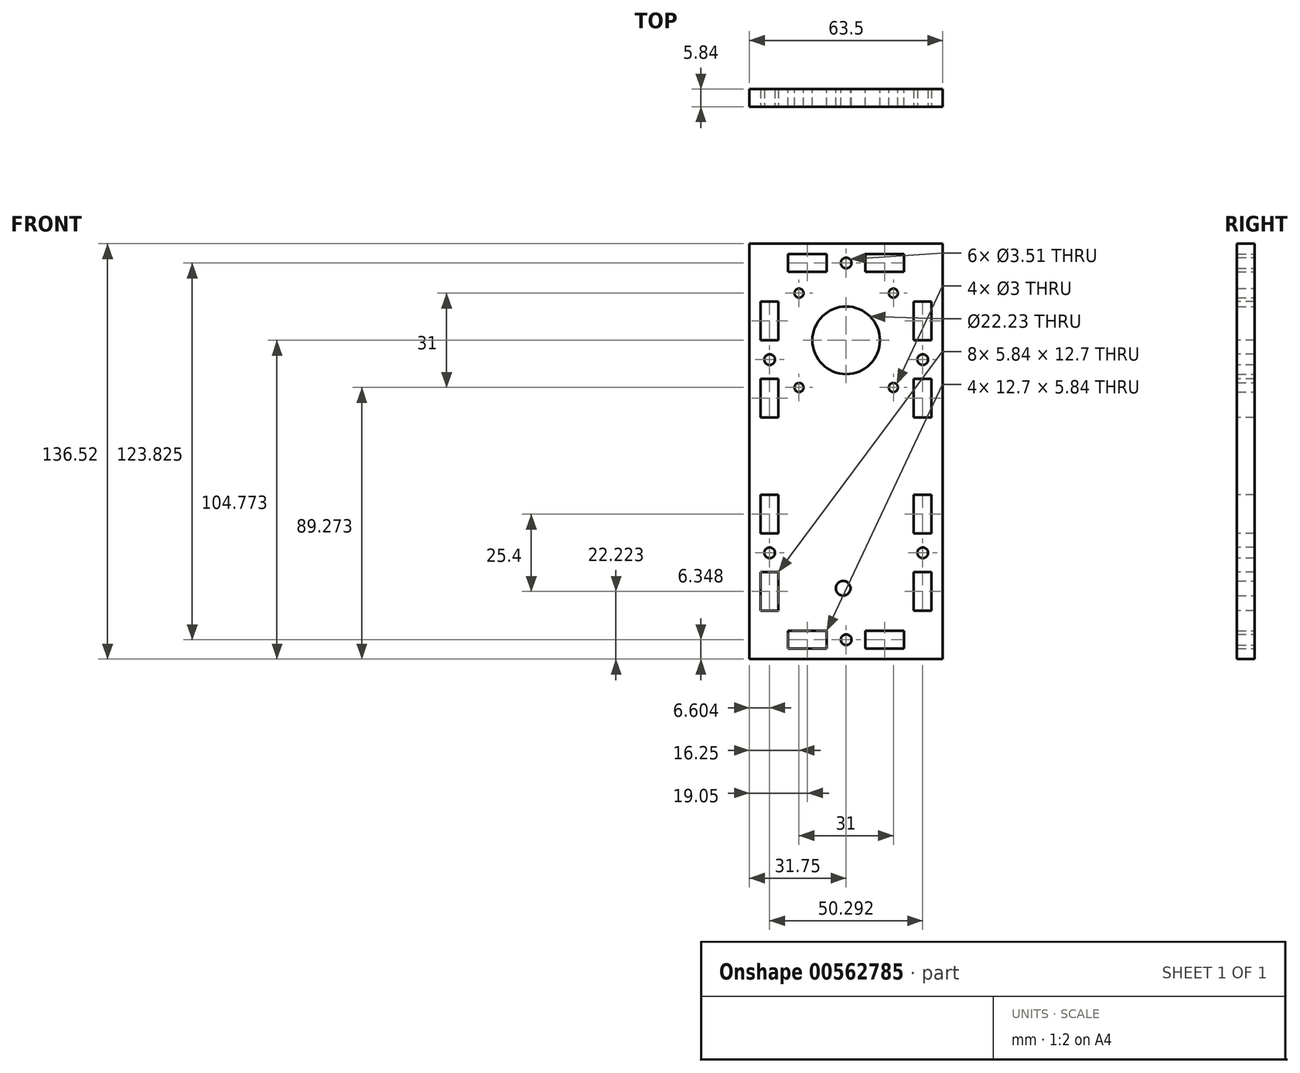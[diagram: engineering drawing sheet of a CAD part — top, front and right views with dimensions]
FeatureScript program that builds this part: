
annotation { "Feature Type Name" : "Feature", "Feature Type Description" : "" }
export const myFeature = defineFeature(function(context is Context, id is Id, definition is map)
    precondition{}
    {
        {
            var Q0;
            Q0=qCreatedBy(makeId("Front.planeOp"),FACE);
            var sketch = newSketch(context, id + "F0", { "sketchPlane" : qUnion([Q0])});
            skLineSegment(sketch, "E0.bottom", {"start": v(-31.75, 68.26) * mm, "end": v(31.75, 68.26) * mm});
            skLineSegment(sketch, "E0.top", {"start": v(-31.75, -68.26) * mm, "end": v(31.75, -68.26) * mm});
            skLineSegment(sketch, "E0.left", {"start": v(-31.75, 68.26) * mm, "end": v(-31.75, -68.26) * mm});
            skLineSegment(sketch, "E0.right", {"start": v(31.75, 68.26) * mm, "end": v(31.75, -68.26) * mm});
            skPoint(sketch, "E0.middle", {"position": v(0, 0) * mm});
            skCircle(sketch, "E1", {"center": v(0, 36.51) * mm, "radius": 11.11 * mm});
            skCircle(sketch, "E2", {"center": v(15.5, 52.01) * mm, "radius": 1.5 * mm});
            skCircle(sketch, "E3.MirrorC", {"center": v(-15.5, 52.01) * mm, "radius": 1.5 * mm});
            skLineSegment(sketch, "E4", {"start": v(-11.11, 36.51) * mm, "end": v(11.11, 36.51) * mm, "construction": true});
            skCircle(sketch, "E5.MirrorC", {"center": v(15.5, 21.01) * mm, "radius": 1.5 * mm});
            skCircle(sketch, "E6.MirrorC", {"center": v(-15.5, 21.01) * mm, "radius": 1.5 * mm});
            skLineSegment(sketch, "E7", {"start": v(-31.75, 61.91) * mm, "end": v(31.75, 61.91) * mm, "construction": true});
            skLineSegment(sketch, "E8.bottom", {"start": v(-6.35, 64.83) * mm, "end": v(-19.05, 64.83) * mm});
            skLineSegment(sketch, "E8.top", {"start": v(-6.35, 59) * mm, "end": v(-19.05, 59) * mm});
            skLineSegment(sketch, "E8.left", {"start": v(-6.35, 64.83) * mm, "end": v(-6.35, 59) * mm});
            skLineSegment(sketch, "E8.right", {"start": v(-19.05, 64.83) * mm, "end": v(-19.05, 59) * mm});
            skPoint(sketch, "E8.middle", {"position": v(-12.7, 61.91) * mm});
            skLineSegment(sketch, "E9.MirrorCS", {"start": v(19.05, 64.83) * mm, "end": v(19.05, 59) * mm});
            skLineSegment(sketch, "E10.MirrorCS", {"start": v(6.35, 64.83) * mm, "end": v(6.35, 59) * mm});
            skPoint(sketch, "E11.MirrorP", {"position": v(12.7, 61.91) * mm});
            skLineSegment(sketch, "E12.MirrorCS", {"start": v(6.35, 59) * mm, "end": v(19.05, 59) * mm});
            skLineSegment(sketch, "E13.MirrorCS", {"start": v(6.35, 64.83) * mm, "end": v(19.05, 64.83) * mm});
            skLineSegment(sketch, "E14.bottom", {"start": v(-21, 57.51) * mm, "end": v(21, 57.51) * mm, "construction": true});
            skLineSegment(sketch, "E14.top", {"start": v(-21, 15.51) * mm, "end": v(21, 15.51) * mm, "construction": true});
            skLineSegment(sketch, "E14.left", {"start": v(-21, 57.51) * mm, "end": v(-21, 15.51) * mm, "construction": true});
            skLineSegment(sketch, "E14.right", {"start": v(21, 57.51) * mm, "end": v(21, 15.51) * mm, "construction": true});
            skCircle(sketch, "E15", {"center": v(0, 61.91) * mm, "radius": 1.75 * mm});
            skLineSegment(sketch, "E16", {"start": v(-31.75, 0) * mm, "end": v(31.75, 0) * mm, "construction": true});
            skLineSegment(sketch, "E17.MirrorCS", {"start": v(6.35, -64.83) * mm, "end": v(6.35, -59) * mm});
            skCircle(sketch, "E18.MirrorC", {"center": v(0, -61.91) * mm, "radius": 1.75 * mm});
            skLineSegment(sketch, "E19.MirrorCS", {"start": v(19.05, -64.83) * mm, "end": v(19.05, -59) * mm});
            skLineSegment(sketch, "E20.MirrorCS", {"start": v(-19.05, -64.83) * mm, "end": v(-19.05, -59) * mm});
            skLineSegment(sketch, "E21.MirrorCS", {"start": v(-6.35, -64.83) * mm, "end": v(-6.35, -59) * mm});
            skLineSegment(sketch, "E22.MirrorCS", {"start": v(6.35, -64.83) * mm, "end": v(19.05, -64.83) * mm});
            skLineSegment(sketch, "E23.MirrorCS", {"start": v(-6.35, -59) * mm, "end": v(-19.05, -59) * mm});
            skLineSegment(sketch, "E24.MirrorCS", {"start": v(-6.35, -64.83) * mm, "end": v(-19.05, -64.83) * mm});
            skLineSegment(sketch, "E25.MirrorCS", {"start": v(-31.75, -61.91) * mm, "end": v(31.75, -61.91) * mm, "construction": true});
            skLineSegment(sketch, "E26.MirrorCS", {"start": v(6.35, -59) * mm, "end": v(19.05, -59) * mm});
            skLineSegment(sketch, "E27.MirrorCS", {"start": v(-21, -57.51) * mm, "end": v(21, -57.51) * mm, "construction": true});
            skPoint(sketch, "E28.MirrorP", {"position": v(-12.7, -61.91) * mm});
            skPoint(sketch, "E29.MirrorP", {"position": v(12.7, -61.91) * mm});
            skCircle(sketch, "E30", {"center": v(-1, -44.99) * mm, "radius": 2.41 * mm});
            skCircle(sketch, "E31", {"center": v(-1, -44.99) * mm, "radius": 8 * mm, "construction": true});
            skSolve(sketch);
        }
        {
            var Q0;
            Q0 = qSketchRegion(id + "F0", true);
            extrude(context, id + "F1", {"entities" : qUnion([Q0]), "depth" : 5.84 * mm, "offsetDistance" : 25.4 * mm});
        }
        {
            var Q0;
            Q0=makeQuery(id+"F1.opExtrude","CAP_FACE",FACE,{"disambiguationData":[OSD([sQuery(id+"F0.wireOp",EDGE,"E0.bottom"),sQuery(id+"F0.wireOp",EDGE,"E0.top"),sQuery(id+"F0.wireOp",EDGE,"E0.left"),sQuery(id+"F0.wireOp",EDGE,"E0.right"),sQuery(id+"F0.wireOp",EDGE,"E1"),sQuery(id+"F0.wireOp",EDGE,"E2"),sQuery(id+"F0.wireOp",EDGE,"E3.MirrorC"),sQuery(id+"F0.wireOp",EDGE,"E5.MirrorC"),sQuery(id+"F0.wireOp",EDGE,"E6.MirrorC"),sQuery(id+"F0.wireOp",EDGE,"E8.bottom"),sQuery(id+"F0.wireOp",EDGE,"E8.top"),sQuery(id+"F0.wireOp",EDGE,"E8.left"),sQuery(id+"F0.wireOp",EDGE,"E8.right"),sQuery(id+"F0.wireOp",EDGE,"E9.MirrorCS"),sQuery(id+"F0.wireOp",EDGE,"E10.MirrorCS"),sQuery(id+"F0.wireOp",EDGE,"E12.MirrorCS"),sQuery(id+"F0.wireOp",EDGE,"E13.MirrorCS"),sQuery(id+"F0.wireOp",EDGE,"E15"),sQuery(id+"F0.wireOp",EDGE,"E17.MirrorCS"),sQuery(id+"F0.wireOp",EDGE,"E18.MirrorC"),sQuery(id+"F0.wireOp",EDGE,"E19.MirrorCS"),sQuery(id+"F0.wireOp",EDGE,"E20.MirrorCS"),sQuery(id+"F0.wireOp",EDGE,"E21.MirrorCS"),sQuery(id+"F0.wireOp",EDGE,"E22.MirrorCS"),sQuery(id+"F0.wireOp",EDGE,"E23.MirrorCS"),sQuery(id+"F0.wireOp",EDGE,"E24.MirrorCS"),sQuery(id+"F0.wireOp",EDGE,"E26.MirrorCS"),sQuery(id+"F0.wireOp",EDGE,"E30")])],"isStart":false});
            var sketch = newSketch(context, id + "F2", { "sketchPlane" : qUnion([Q0])});
            skLineSegment(sketch, "E32.bottom", {"start": v(-28.07, 36.51) * mm, "end": v(-22.23, 36.51) * mm});
            skLineSegment(sketch, "E32.top", {"start": v(-28.07, 49.21) * mm, "end": v(-22.23, 49.21) * mm});
            skLineSegment(sketch, "E32.left", {"start": v(-28.07, 36.51) * mm, "end": v(-28.07, 49.21) * mm});
            skLineSegment(sketch, "E32.right", {"start": v(-22.23, 36.51) * mm, "end": v(-22.23, 49.21) * mm});
            skPoint(sketch, "E32.middle", {"position": v(-25.15, 42.86) * mm});
            skLineSegment(sketch, "E33", {"start": v(-25.15, 42.86) * mm, "end": v(-25.15, 0) * mm, "construction": true});
            skLineSegment(sketch, "E34.bottom", {"start": v(-22.23, 23.81) * mm, "end": v(-28.07, 23.81) * mm});
            skLineSegment(sketch, "E34.top", {"start": v(-22.23, 11.11) * mm, "end": v(-28.07, 11.11) * mm});
            skLineSegment(sketch, "E34.left", {"start": v(-22.23, 23.81) * mm, "end": v(-22.23, 11.11) * mm});
            skLineSegment(sketch, "E34.right", {"start": v(-28.07, 23.81) * mm, "end": v(-28.07, 11.11) * mm});
            skPoint(sketch, "E34.middle", {"position": v(-25.15, 17.46) * mm});
            skCircle(sketch, "E35", {"center": v(-25.15, 30.16) * mm, "radius": 1.75 * mm});
            skLineSegment(sketch, "E36.MirrorCS", {"start": v(22.23, 11.11) * mm, "end": v(28.07, 11.11) * mm});
            skLineSegment(sketch, "E37.MirrorCS", {"start": v(22.23, 23.81) * mm, "end": v(28.07, 23.81) * mm});
            skLineSegment(sketch, "E38.MirrorCS", {"start": v(22.23, 36.51) * mm, "end": v(22.23, 49.21) * mm});
            skLineSegment(sketch, "E39.MirrorCS", {"start": v(28.07, 36.51) * mm, "end": v(28.07, 49.21) * mm});
            skLineSegment(sketch, "E40.MirrorCS", {"start": v(28.07, 49.21) * mm, "end": v(22.23, 49.21) * mm});
            skLineSegment(sketch, "E41.MirrorCS", {"start": v(28.07, 36.51) * mm, "end": v(22.23, 36.51) * mm});
            skLineSegment(sketch, "E42.MirrorCS", {"start": v(22.23, 23.81) * mm, "end": v(22.23, 11.11) * mm});
            skPoint(sketch, "E43.MirrorP", {"position": v(25.15, 17.46) * mm});
            skPoint(sketch, "E44.MirrorP", {"position": v(25.15, 42.86) * mm});
            skLineSegment(sketch, "E45.MirrorCS", {"start": v(28.07, 23.81) * mm, "end": v(28.07, 11.11) * mm});
            skCircle(sketch, "E46.MirrorC", {"center": v(25.15, 30.16) * mm, "radius": 1.75 * mm});
            skLineSegment(sketch, "E47.MirrorCS", {"start": v(25.15, 42.86) * mm, "end": v(25.15, 0) * mm, "construction": true});
            skLineSegment(sketch, "E48.bottom", {"start": v(-22.23, -14.29) * mm, "end": v(-28.07, -14.29) * mm});
            skLineSegment(sketch, "E48.top", {"start": v(-22.23, -26.99) * mm, "end": v(-28.07, -26.99) * mm});
            skLineSegment(sketch, "E48.left", {"start": v(-22.23, -14.29) * mm, "end": v(-22.23, -26.99) * mm});
            skLineSegment(sketch, "E48.right", {"start": v(-28.07, -14.29) * mm, "end": v(-28.07, -26.99) * mm});
            skPoint(sketch, "E48.middle", {"position": v(-25.15, -20.64) * mm});
            skCircle(sketch, "E49", {"center": v(-25.15, -33.34) * mm, "radius": 1.75 * mm});
            skLineSegment(sketch, "E50.bottom", {"start": v(-28.07, -39.69) * mm, "end": v(-22.23, -39.69) * mm});
            skLineSegment(sketch, "E50.top", {"start": v(-28.07, -52.39) * mm, "end": v(-22.23, -52.39) * mm});
            skLineSegment(sketch, "E50.left", {"start": v(-28.07, -39.69) * mm, "end": v(-28.07, -52.39) * mm});
            skLineSegment(sketch, "E50.right", {"start": v(-22.23, -39.69) * mm, "end": v(-22.23, -52.39) * mm});
            skPoint(sketch, "E50.middle", {"position": v(-25.15, -46.04) * mm});
            skLineSegment(sketch, "E51.MirrorCS", {"start": v(28.07, -14.29) * mm, "end": v(28.07, -26.99) * mm});
            skLineSegment(sketch, "E52.MirrorCS", {"start": v(22.23, -14.29) * mm, "end": v(22.23, -26.99) * mm});
            skLineSegment(sketch, "E53.MirrorCS", {"start": v(22.23, -14.29) * mm, "end": v(28.07, -14.29) * mm});
            skLineSegment(sketch, "E54.MirrorCS", {"start": v(28.07, -39.69) * mm, "end": v(22.23, -39.69) * mm});
            skLineSegment(sketch, "E55.MirrorCS", {"start": v(22.23, -26.99) * mm, "end": v(28.07, -26.99) * mm});
            skPoint(sketch, "E56.MirrorP", {"position": v(25.15, -46.04) * mm});
            skLineSegment(sketch, "E57.MirrorCS", {"start": v(22.23, -39.69) * mm, "end": v(22.23, -52.39) * mm});
            skCircle(sketch, "E58.MirrorC", {"center": v(25.15, -33.34) * mm, "radius": 1.75 * mm});
            skPoint(sketch, "E59.MirrorP", {"position": v(25.15, -20.64) * mm});
            skLineSegment(sketch, "E60.MirrorCS", {"start": v(28.07, -52.39) * mm, "end": v(22.23, -52.39) * mm});
            skLineSegment(sketch, "E61.MirrorCS", {"start": v(28.07, -39.69) * mm, "end": v(28.07, -52.39) * mm});
            skSolve(sketch);
        }
        {
            var Q0;
            Q0 = qSketchRegion(id + "F2", true);
            extrude(context, id + "F3", {"entities" : qUnion([Q0]), "operationType" : NewBodyOperationType.REMOVE, "oppositeDirection" : true, "depth" : 25.4 * mm, "offsetDistance" : 25.4 * mm});
        }
    });
